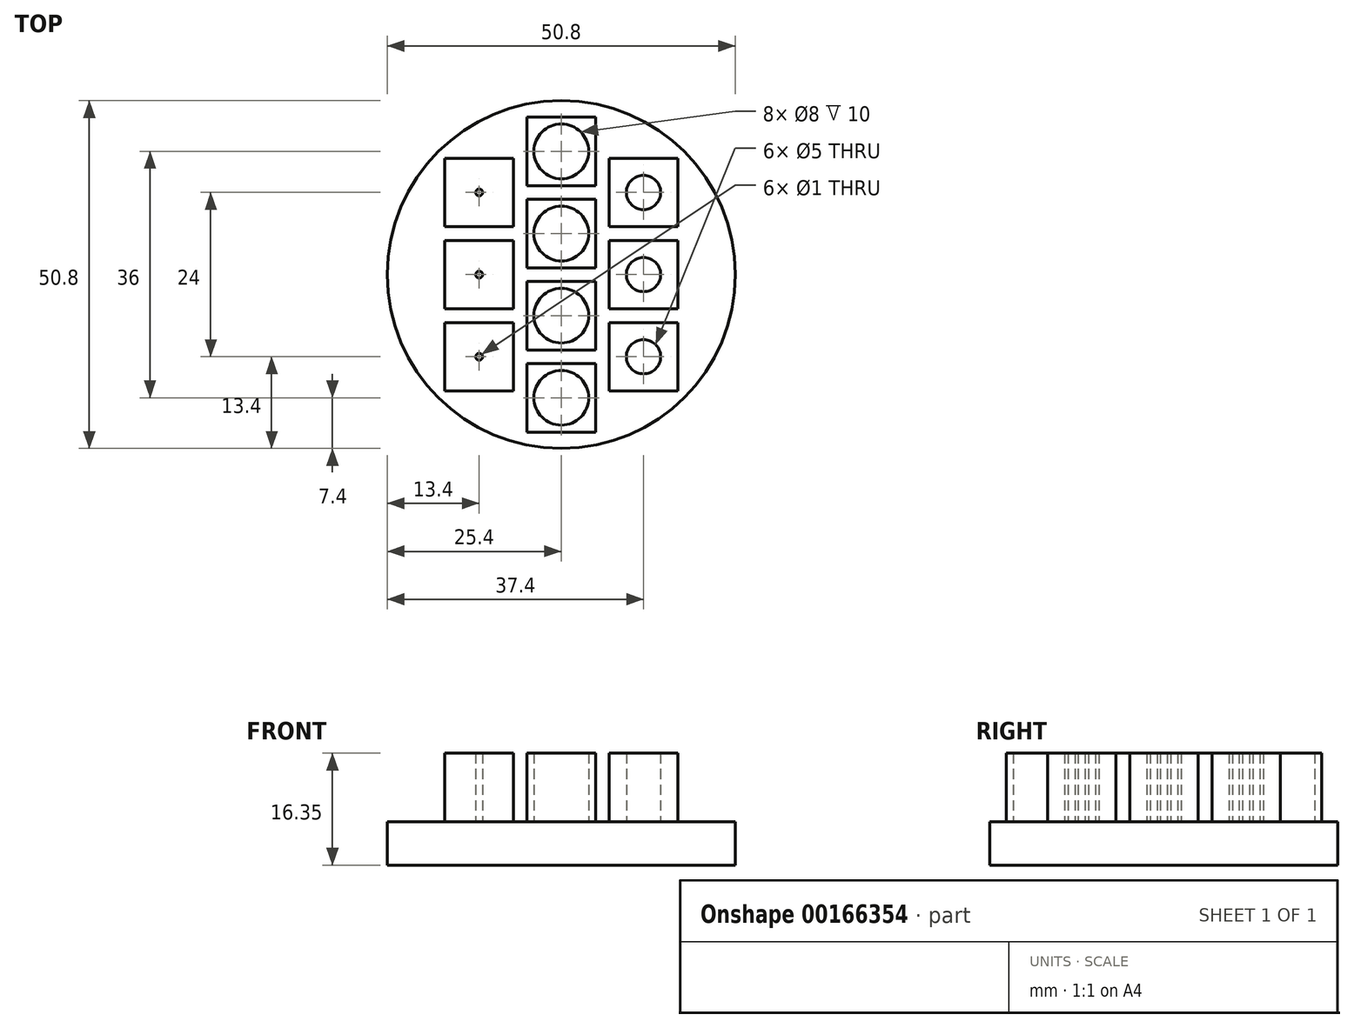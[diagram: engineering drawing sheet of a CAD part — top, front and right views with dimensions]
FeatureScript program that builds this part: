
annotation { "Feature Type Name" : "Feature", "Feature Type Description" : "" }
export const myFeature = defineFeature(function(context is Context, id is Id, definition is map)
    precondition{}
    {
        {
            var Q0;
            Q0=qCreatedBy(makeId("Top.planeOp"),FACE);
            var sketch = newSketch(context, id + "F0", { "sketchPlane" : qUnion([Q0])});
            skCircle(sketch, "E0", {"center": v(0, 0) * mm, "radius": 25.4 * mm});
            skLineSegment(sketch, "E1", {"start": v(0, 25.4) * mm, "end": v(0, -25.4) * mm, "construction": true});
            skLineSegment(sketch, "E2", {"start": v(-25.4, 0) * mm, "end": v(25.4, 0) * mm, "construction": true});
            skLineSegment(sketch, "E3", {"start": v(5, -24.9) * mm, "end": v(5, 24.9) * mm, "construction": true});
            skLineSegment(sketch, "E4", {"start": v(-5, 24.9) * mm, "end": v(-5, -24.9) * mm, "construction": true});
            skLineSegment(sketch, "E5.bottom", {"start": v(7, 5) * mm, "end": v(17, 5) * mm});
            skLineSegment(sketch, "E5.top", {"start": v(7, -5) * mm, "end": v(17, -5) * mm});
            skLineSegment(sketch, "E5.left", {"start": v(7, 5) * mm, "end": v(7, -5) * mm});
            skLineSegment(sketch, "E5.right", {"start": v(17, 5) * mm, "end": v(17, -5) * mm});
            skLineSegment(sketch, "E6", {"start": v(12, 5) * mm, "end": v(12, -5) * mm, "construction": true});
            skLineSegment(sketch, "E7", {"start": v(7, 0) * mm, "end": v(17, 0) * mm, "construction": true});
            skLineSegment(sketch, "E8.bottom", {"start": v(-5, 11) * mm, "end": v(5, 11) * mm});
            skLineSegment(sketch, "E8.top", {"start": v(-5, 1) * mm, "end": v(5, 1) * mm});
            skLineSegment(sketch, "E8.left", {"start": v(-5, 11) * mm, "end": v(-5, 1) * mm});
            skLineSegment(sketch, "E8.right", {"start": v(5, 11) * mm, "end": v(5, 1) * mm});
            skLineSegment(sketch, "E9", {"start": v(0, 11) * mm, "end": v(0, 1) * mm, "construction": true});
            skLineSegment(sketch, "E10", {"start": v(-5, 6) * mm, "end": v(5, 6) * mm, "construction": true});
            skLineSegment(sketch, "E11.bottom", {"start": v(-5, 23) * mm, "end": v(5, 23) * mm});
            skLineSegment(sketch, "E11.top", {"start": v(-5, 13) * mm, "end": v(5, 13) * mm});
            skLineSegment(sketch, "E11.left", {"start": v(-5, 23) * mm, "end": v(-5, 13) * mm});
            skLineSegment(sketch, "E11.right", {"start": v(5, 23) * mm, "end": v(5, 13) * mm});
            skLineSegment(sketch, "E12", {"start": v(0, 23) * mm, "end": v(0, 13) * mm, "construction": true});
            skLineSegment(sketch, "E13", {"start": v(-5, 18) * mm, "end": v(5, 18) * mm, "construction": true});
            skLineSegment(sketch, "E14.bottom", {"start": v(-5, -1) * mm, "end": v(5, -1) * mm});
            skLineSegment(sketch, "E14.top", {"start": v(-5, -11) * mm, "end": v(5, -11) * mm});
            skLineSegment(sketch, "E14.left", {"start": v(-5, -1) * mm, "end": v(-5, -11) * mm});
            skLineSegment(sketch, "E14.right", {"start": v(5, -1) * mm, "end": v(5, -11) * mm});
            skLineSegment(sketch, "E15", {"start": v(0, -1) * mm, "end": v(0, -11) * mm, "construction": true});
            skLineSegment(sketch, "E16", {"start": v(-5, -6) * mm, "end": v(5, -6) * mm, "construction": true});
            skLineSegment(sketch, "E17.bottom", {"start": v(-5, -13) * mm, "end": v(5, -13) * mm});
            skLineSegment(sketch, "E17.top", {"start": v(-5, -23) * mm, "end": v(5, -23) * mm});
            skLineSegment(sketch, "E17.left", {"start": v(-5, -13) * mm, "end": v(-5, -23) * mm});
            skLineSegment(sketch, "E17.right", {"start": v(5, -13) * mm, "end": v(5, -23) * mm});
            skLineSegment(sketch, "E18", {"start": v(0, -13) * mm, "end": v(0, -23) * mm, "construction": true});
            skLineSegment(sketch, "E19", {"start": v(-5, -18) * mm, "end": v(5, -18) * mm, "construction": true});
            skLineSegment(sketch, "E20.bottom", {"start": v(7, -7) * mm, "end": v(17, -7) * mm});
            skLineSegment(sketch, "E20.top", {"start": v(7, -17) * mm, "end": v(17, -17) * mm});
            skLineSegment(sketch, "E20.left", {"start": v(7, -7) * mm, "end": v(7, -17) * mm});
            skLineSegment(sketch, "E20.right", {"start": v(17, -7) * mm, "end": v(17, -17) * mm});
            skLineSegment(sketch, "E21", {"start": v(12, -7) * mm, "end": v(12, -17) * mm, "construction": true});
            skLineSegment(sketch, "E22", {"start": v(7, -12) * mm, "end": v(17, -12) * mm, "construction": true});
            skLineSegment(sketch, "E23.bottom", {"start": v(7, 17) * mm, "end": v(17, 17) * mm});
            skLineSegment(sketch, "E23.top", {"start": v(7, 7) * mm, "end": v(17, 7) * mm});
            skLineSegment(sketch, "E23.left", {"start": v(7, 17) * mm, "end": v(7, 7) * mm});
            skLineSegment(sketch, "E23.right", {"start": v(17, 17) * mm, "end": v(17, 7) * mm});
            skLineSegment(sketch, "E24", {"start": v(12, 17) * mm, "end": v(12, 7) * mm, "construction": true});
            skLineSegment(sketch, "E25", {"start": v(7, 12) * mm, "end": v(17, 12) * mm, "construction": true});
            skLineSegment(sketch, "E26.bottom", {"start": v(-17, 17) * mm, "end": v(-7, 17) * mm});
            skLineSegment(sketch, "E26.top", {"start": v(-17, 7) * mm, "end": v(-7, 7) * mm});
            skLineSegment(sketch, "E26.left", {"start": v(-17, 17) * mm, "end": v(-17, 7) * mm});
            skLineSegment(sketch, "E26.right", {"start": v(-7, 17) * mm, "end": v(-7, 7) * mm});
            skLineSegment(sketch, "E27", {"start": v(-12, 17) * mm, "end": v(-12, 7) * mm, "construction": true});
            skLineSegment(sketch, "E28", {"start": v(-17, 12) * mm, "end": v(-7, 12) * mm, "construction": true});
            skLineSegment(sketch, "E29.bottom", {"start": v(-17, 5) * mm, "end": v(-7, 5) * mm});
            skLineSegment(sketch, "E29.top", {"start": v(-17, -5) * mm, "end": v(-7, -5) * mm});
            skLineSegment(sketch, "E29.left", {"start": v(-17, 5) * mm, "end": v(-17, -5) * mm});
            skLineSegment(sketch, "E29.right", {"start": v(-7, 5) * mm, "end": v(-7, -5) * mm});
            skLineSegment(sketch, "E30", {"start": v(-12, 5) * mm, "end": v(-12, -5) * mm, "construction": true});
            skLineSegment(sketch, "E31", {"start": v(-17, 0) * mm, "end": v(-7, 0) * mm, "construction": true});
            skLineSegment(sketch, "E32.bottom", {"start": v(-17, -7) * mm, "end": v(-7, -7) * mm});
            skLineSegment(sketch, "E32.top", {"start": v(-17, -17) * mm, "end": v(-7, -17) * mm});
            skLineSegment(sketch, "E32.left", {"start": v(-17, -7) * mm, "end": v(-17, -17) * mm});
            skLineSegment(sketch, "E32.right", {"start": v(-7, -7) * mm, "end": v(-7, -17) * mm});
            skLineSegment(sketch, "E33", {"start": v(-12, -7) * mm, "end": v(-12, -17) * mm, "construction": true});
            skLineSegment(sketch, "E34", {"start": v(-17, -12) * mm, "end": v(-7, -12) * mm, "construction": true});
            skCircle(sketch, "E35", {"center": v(0, 18) * mm, "radius": 4 * mm});
            skCircle(sketch, "E36", {"center": v(12, 12) * mm, "radius": 2.5 * mm});
            skCircle(sketch, "E37", {"center": v(12, 0) * mm, "radius": 2.5 * mm});
            skCircle(sketch, "E38", {"center": v(12, -12) * mm, "radius": 2.5 * mm});
            skCircle(sketch, "E39", {"center": v(0, 6) * mm, "radius": 4 * mm});
            skCircle(sketch, "E40", {"center": v(0, -6) * mm, "radius": 4 * mm});
            skCircle(sketch, "E41", {"center": v(0, -18) * mm, "radius": 4 * mm});
            skCircle(sketch, "E42", {"center": v(-12, -12) * mm, "radius": 0.5 * mm});
            skCircle(sketch, "E43", {"center": v(-12, 0) * mm, "radius": 0.5 * mm});
            skCircle(sketch, "E44", {"center": v(-12, 12) * mm, "radius": 0.5 * mm});
            skSolve(sketch);
        }
        {
            var Q0;
            Q0=makeQuery(id+"F0.imprint","IMPRINT",FACE,{"disambiguationData":[TD([[makeQuery(id+"F0.imprint","IMPRINT",EDGE,{"derivedFrom":sQuery(id+"F0.wireOp",EDGE,"E0")}),1.0]])]});
            var Q1;
            Q1=makeQuery(id+"F0.imprint","IMPRINT",FACE,{"disambiguationData":[TD([[makeQuery(id+"F0.imprint","IMPRINT",EDGE,{"derivedFrom":sQuery(id+"F0.wireOp",EDGE,"E32.bottom")}),-1.0]])]});
            var Q2;
            Q2=makeQuery(id+"F0.imprint","IMPRINT",FACE,{"disambiguationData":[TD([[makeQuery(id+"F0.imprint","IMPRINT",EDGE,{"derivedFrom":sQuery(id+"F0.wireOp",EDGE,"E29.bottom")}),-1.0]])]});
            var Q3;
            Q3=makeQuery(id+"F0.imprint","IMPRINT",FACE,{"disambiguationData":[TD([[makeQuery(id+"F0.imprint","IMPRINT",EDGE,{"derivedFrom":sQuery(id+"F0.wireOp",EDGE,"E26.bottom")}),-1.0]])]});
            var Q4;
            Q4=makeQuery(id+"F0.imprint","IMPRINT",FACE,{"disambiguationData":[TD([[makeQuery(id+"F0.imprint","IMPRINT",EDGE,{"derivedFrom":sQuery(id+"F0.wireOp",EDGE,"E8.bottom")}),-1.0]])]});
            var Q5;
            Q5=makeQuery(id+"F0.imprint","IMPRINT",FACE,{"disambiguationData":[TD([[makeQuery(id+"F0.imprint","IMPRINT",EDGE,{"derivedFrom":sQuery(id+"F0.wireOp",EDGE,"E14.bottom")}),-1.0]])]});
            var Q6;
            Q6=makeQuery(id+"F0.imprint","IMPRINT",FACE,{"disambiguationData":[TD([[makeQuery(id+"F0.imprint","IMPRINT",EDGE,{"derivedFrom":sQuery(id+"F0.wireOp",EDGE,"E17.bottom")}),-1.0]])]});
            var Q7;
            Q7=makeQuery(id+"F0.imprint","IMPRINT",FACE,{"disambiguationData":[TD([[makeQuery(id+"F0.imprint","IMPRINT",EDGE,{"derivedFrom":sQuery(id+"F0.wireOp",EDGE,"E11.bottom")}),-1.0]])]});
            var Q8;
            Q8=makeQuery(id+"F0.imprint","IMPRINT",FACE,{"disambiguationData":[TD([[makeQuery(id+"F0.imprint","IMPRINT",EDGE,{"derivedFrom":sQuery(id+"F0.wireOp",EDGE,"E23.bottom")}),-1.0]])]});
            var Q9;
            Q9=makeQuery(id+"F0.imprint","IMPRINT",FACE,{"disambiguationData":[TD([[makeQuery(id+"F0.imprint","IMPRINT",EDGE,{"derivedFrom":sQuery(id+"F0.wireOp",EDGE,"E5.bottom")}),-1.0]])]});
            var Q10;
            Q10=makeQuery(id+"F0.imprint","IMPRINT",FACE,{"disambiguationData":[TD([[makeQuery(id+"F0.imprint","IMPRINT",EDGE,{"derivedFrom":sQuery(id+"F0.wireOp",EDGE,"E20.bottom")}),-1.0]])]});
            var Q11;
            Q11=makeQuery(id+"F0.imprint","IMPRINT",FACE,{"disambiguationData":[TD([[makeQuery(id+"F0.imprint","IMPRINT",EDGE,{"derivedFrom":sQuery(id+"F0.wireOp",EDGE,"E42")}),1.0]])]});
            var Q12;
            Q12=makeQuery(id+"F0.imprint","IMPRINT",FACE,{"disambiguationData":[TD([[makeQuery(id+"F0.imprint","IMPRINT",EDGE,{"derivedFrom":sQuery(id+"F0.wireOp",EDGE,"E43")}),1.0]])]});
            var Q13;
            Q13=makeQuery(id+"F0.imprint","IMPRINT",FACE,{"disambiguationData":[TD([[makeQuery(id+"F0.imprint","IMPRINT",EDGE,{"derivedFrom":sQuery(id+"F0.wireOp",EDGE,"E44")}),1.0]])]});
            var Q14;
            Q14=makeQuery(id+"F0.imprint","IMPRINT",FACE,{"disambiguationData":[TD([[makeQuery(id+"F0.imprint","IMPRINT",EDGE,{"derivedFrom":sQuery(id+"F0.wireOp",EDGE,"E35")}),1.0]])]});
            var Q15;
            Q15=makeQuery(id+"F0.imprint","IMPRINT",FACE,{"disambiguationData":[TD([[makeQuery(id+"F0.imprint","IMPRINT",EDGE,{"derivedFrom":sQuery(id+"F0.wireOp",EDGE,"E39")}),1.0]])]});
            var Q16;
            Q16=makeQuery(id+"F0.imprint","IMPRINT",FACE,{"disambiguationData":[TD([[makeQuery(id+"F0.imprint","IMPRINT",EDGE,{"derivedFrom":sQuery(id+"F0.wireOp",EDGE,"E41")}),1.0]])]});
            var Q17;
            Q17=makeQuery(id+"F0.imprint","IMPRINT",FACE,{"disambiguationData":[TD([[makeQuery(id+"F0.imprint","IMPRINT",EDGE,{"derivedFrom":sQuery(id+"F0.wireOp",EDGE,"E38")}),1.0]])]});
            var Q18;
            Q18=makeQuery(id+"F0.imprint","IMPRINT",FACE,{"disambiguationData":[TD([[makeQuery(id+"F0.imprint","IMPRINT",EDGE,{"derivedFrom":sQuery(id+"F0.wireOp",EDGE,"E37")}),1.0]])]});
            var Q19;
            Q19=makeQuery(id+"F0.imprint","IMPRINT",FACE,{"disambiguationData":[TD([[makeQuery(id+"F0.imprint","IMPRINT",EDGE,{"derivedFrom":sQuery(id+"F0.wireOp",EDGE,"E36")}),1.0]])]});
            var Q20;
            Q20=makeQuery(id+"F0.imprint","IMPRINT",FACE,{"disambiguationData":[TD([[makeQuery(id+"F0.imprint","IMPRINT",EDGE,{"derivedFrom":sQuery(id+"F0.wireOp",EDGE,"E40")}),1.0]])]});
            extrude(context, id + "F1", {"entities" : qUnion([Q0, Q1, Q2, Q3, Q4, Q5, Q6, Q7, Q8, Q9, Q10, Q11, Q12, Q13, Q14, Q15, Q16, Q17, Q18, Q19, Q20]), "oppositeDirection" : true, "depth" : 6.35 * mm});
        }
        {
            var Q0;
            Q0=makeQuery(id+"F0.imprint","IMPRINT",FACE,{"disambiguationData":[TD([[makeQuery(id+"F0.imprint","IMPRINT",EDGE,{"derivedFrom":sQuery(id+"F0.wireOp",EDGE,"E26.bottom")}),-1.0]])]});
            var Q1;
            Q1=makeQuery(id+"F0.imprint","IMPRINT",FACE,{"disambiguationData":[TD([[makeQuery(id+"F0.imprint","IMPRINT",EDGE,{"derivedFrom":sQuery(id+"F0.wireOp",EDGE,"E11.bottom")}),-1.0]])]});
            var Q2;
            Q2=makeQuery(id+"F0.imprint","IMPRINT",FACE,{"disambiguationData":[TD([[makeQuery(id+"F0.imprint","IMPRINT",EDGE,{"derivedFrom":sQuery(id+"F0.wireOp",EDGE,"E23.bottom")}),-1.0]])]});
            var Q3;
            Q3=makeQuery(id+"F0.imprint","IMPRINT",FACE,{"disambiguationData":[TD([[makeQuery(id+"F0.imprint","IMPRINT",EDGE,{"derivedFrom":sQuery(id+"F0.wireOp",EDGE,"E8.bottom")}),-1.0]])]});
            var Q4;
            Q4=makeQuery(id+"F0.imprint","IMPRINT",FACE,{"disambiguationData":[TD([[makeQuery(id+"F0.imprint","IMPRINT",EDGE,{"derivedFrom":sQuery(id+"F0.wireOp",EDGE,"E29.bottom")}),-1.0]])]});
            var Q5;
            Q5=makeQuery(id+"F0.imprint","IMPRINT",FACE,{"disambiguationData":[TD([[makeQuery(id+"F0.imprint","IMPRINT",EDGE,{"derivedFrom":sQuery(id+"F0.wireOp",EDGE,"E32.bottom")}),-1.0]])]});
            var Q6;
            Q6=makeQuery(id+"F0.imprint","IMPRINT",FACE,{"disambiguationData":[TD([[makeQuery(id+"F0.imprint","IMPRINT",EDGE,{"derivedFrom":sQuery(id+"F0.wireOp",EDGE,"E14.bottom")}),-1.0]])]});
            var Q7;
            Q7=makeQuery(id+"F0.imprint","IMPRINT",FACE,{"disambiguationData":[TD([[makeQuery(id+"F0.imprint","IMPRINT",EDGE,{"derivedFrom":sQuery(id+"F0.wireOp",EDGE,"E17.bottom")}),-1.0]])]});
            var Q8;
            Q8=makeQuery(id+"F0.imprint","IMPRINT",FACE,{"disambiguationData":[TD([[makeQuery(id+"F0.imprint","IMPRINT",EDGE,{"derivedFrom":sQuery(id+"F0.wireOp",EDGE,"E5.bottom")}),-1.0]])]});
            var Q9;
            Q9=makeQuery(id+"F0.imprint","IMPRINT",FACE,{"disambiguationData":[TD([[makeQuery(id+"F0.imprint","IMPRINT",EDGE,{"derivedFrom":sQuery(id+"F0.wireOp",EDGE,"E20.bottom")}),-1.0]])]});
            extrude(context, id + "F2", {"entities" : qUnion([Q0, Q1, Q2, Q3, Q4, Q5, Q6, Q7, Q8, Q9]), "depth" : 10 * mm});
        }
    });
